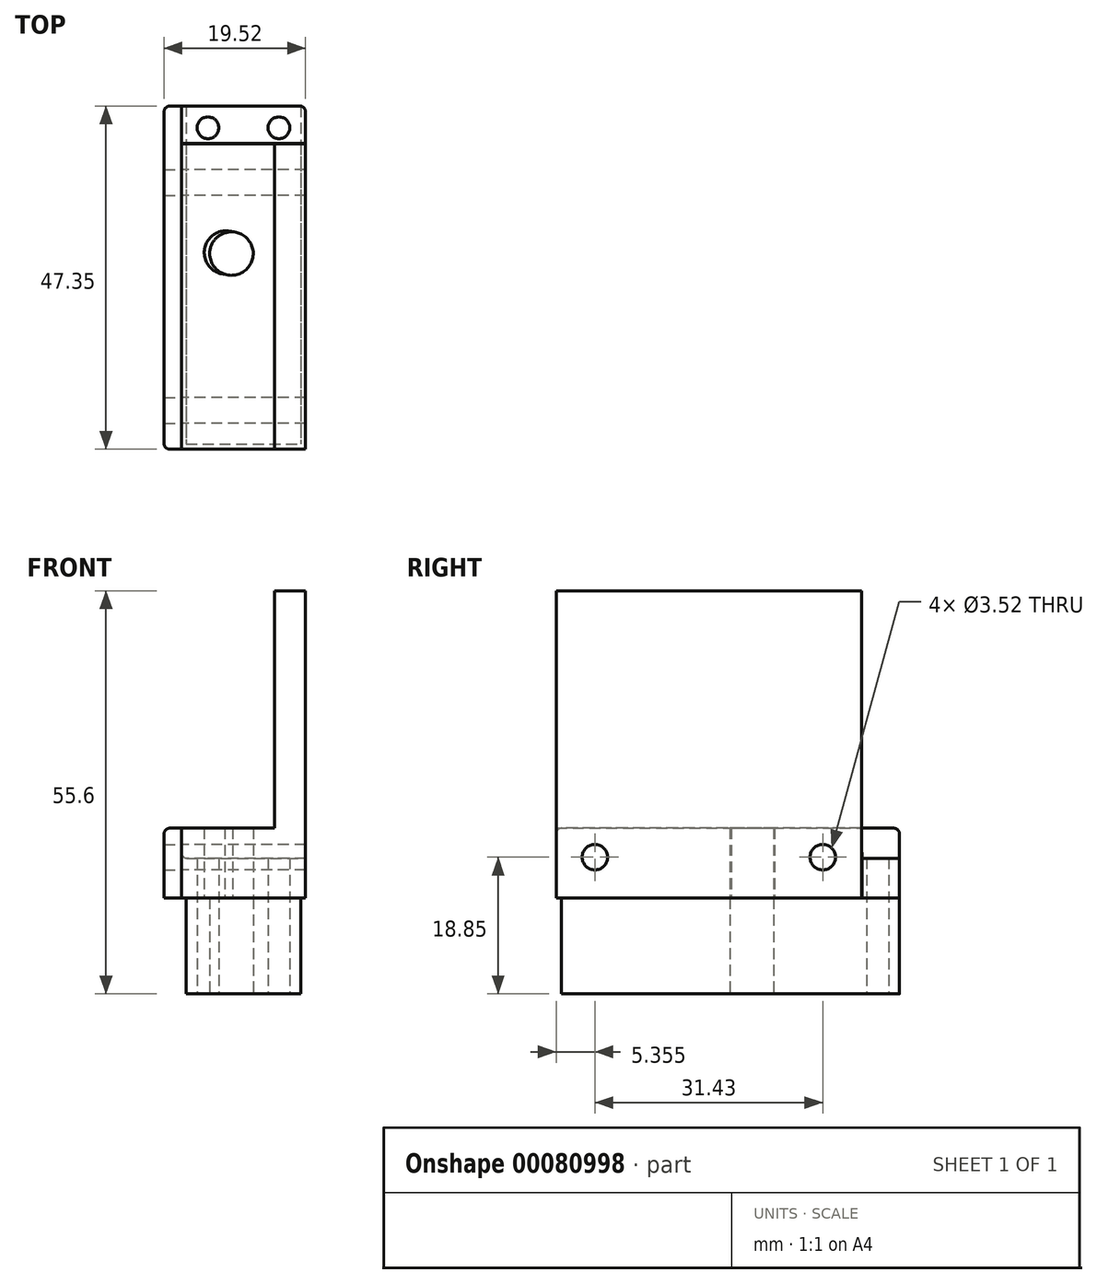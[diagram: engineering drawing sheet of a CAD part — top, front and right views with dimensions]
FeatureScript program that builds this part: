
annotation { "Feature Type Name" : "Feature", "Feature Type Description" : "" }
export const myFeature = defineFeature(function(context is Context, id is Id, definition is map)
    precondition{}
    {
        {
            var Q0;
            Q0=qCreatedBy(makeId("Top.planeOp"),FACE);
            var sketch = newSketch(context, id + "F0", { "sketchPlane" : qUnion([Q0])});
            skLineSegment(sketch, "E0.bottom", {"start": v(-8.56, 21.06) * mm, "end": v(8.56, 21.06) * mm});
            skLineSegment(sketch, "E0.top", {"start": v(-8.56, -21.07) * mm, "end": v(8.55, -21.07) * mm});
            skLineSegment(sketch, "E0.left", {"start": v(-8.56, 21.06) * mm, "end": v(-8.56, -21.07) * mm});
            skLineSegment(sketch, "E0.right", {"start": v(8.56, 21.06) * mm, "end": v(8.55, -21.07) * mm});
            skLineSegment(sketch, "E1", {"start": v(-8.55, 21.06) * mm, "end": v(8.56, -21.07) * mm, "construction": true});
            skSolve(sketch);
        }
        {
            var Q0;
            Q0=makeQuery(id+"F0.imprint","IMPRINT",FACE,{"disambiguationData":[TD([[makeQuery(id+"F0.imprint","IMPRINT",EDGE,{"derivedFrom":sQuery(id+"F0.wireOp",EDGE,"E0.bottom")}),-1.0]])]});
            extrude(context, id + "F1", {"entities" : qUnion([Q0]), "depth" : 9.65 * mm});
        }
        {
            var Q0;
            Q0=makeQuery(id+"F1.opExtrude","SWEPT_FACE",FACE,{"disambiguationData":[OSD([sQuery(id+"F0.wireOp",EDGE,"E0.left")])]});
            var sketch = newSketch(context, id + "F2", { "sketchPlane" : qUnion([Q0])});
            skCircle(sketch, "E2", {"center": v(-15.71, 5.65) * mm, "radius": 1.76 * mm});
            skLineSegment(sketch, "E3", {"start": v(0, 9.65) * mm, "end": v(0, 0) * mm, "construction": true});
            skCircle(sketch, "E4.MirrorC", {"center": v(15.71, 5.65) * mm, "radius": 1.76 * mm});
            skSolve(sketch);
        }
        {
            var Q0;
            Q0=makeQuery(id+"F1.opExtrude","SWEPT_FACE",FACE,{"disambiguationData":[OSD([sQuery(id+"F0.wireOp",EDGE,"E0.right")])]});
            var sketch = newSketch(context, id + "F3", { "sketchPlane" : qUnion([Q0])});
            skPoint(sketch, "E5", {"position": v(-21.07, 0) * mm});
            skPoint(sketch, "E6", {"position": v(21.06, 0) * mm});
            skLineSegment(sketch, "E7.bottom", {"start": v(-21.07, 0) * mm, "end": v(21.07, 0) * mm});
            skLineSegment(sketch, "E7.top", {"start": v(-21.07, 42.4) * mm, "end": v(21.06, 42.4) * mm});
            skLineSegment(sketch, "E7.left", {"start": v(-21.07, 0) * mm, "end": v(-21.07, 42.4) * mm});
            skLineSegment(sketch, "E7.right", {"start": v(21.06, 0) * mm, "end": v(21.06, 42.4) * mm});
            skSolve(sketch);
        }
        {
            var Q0;
            Q0 = qSketchRegion(id + "F3", true);
            extrude(context, id + "F4", {"entities" : qUnion([Q0]), "operationType" : NewBodyOperationType.ADD, "oppositeDirection" : true, "depth" : 4.25 * mm});
        }
        {
            var Q0;
            Q0 = qSketchRegion(id + "F2", true);
            extrude(context, id + "F5", {"entities" : qUnion([Q0]), "operationType" : NewBodyOperationType.REMOVE, "endBound" : BoundingType.THROUGH_ALL, "oppositeDirection" : true, "depth" : 25 * mm});
        }
        {
            var Q0;
            Q0=makeQuery(id+"F1.opExtrude","CAP_FACE",FACE,{"disambiguationData":[OSD([sQuery(id+"F0.wireOp",EDGE,"E0.bottom"),sQuery(id+"F0.wireOp",EDGE,"E0.top"),sQuery(id+"F0.wireOp",EDGE,"E0.left"),sQuery(id+"F0.wireOp",EDGE,"E0.right")])],"isStart":true});
            var sketch = newSketch(context, id + "F6", { "sketchPlane" : qUnion([Q0])});
            skCircle(sketch, "E8", {"center": v(-2.4, -6.06) * mm, "radius": 3 * mm});
            skSolve(sketch);
        }
        {
            var Q0;
            Q0 = qSketchRegion(id + "F6", true);
            extrude(context, id + "F7", {"entities" : qUnion([Q0]), "operationType" : NewBodyOperationType.REMOVE, "oppositeDirection" : true, "depth" : 25 * mm});
        }
        {
            var Q0;
            Q0=qCreatedBy(makeId("Top.planeOp"),FACE);
            var sketch = newSketch(context, id + "F8", { "sketchPlane" : qUnion([Q0])});
            skLineSegment(sketch, "E9.bottom", {"start": v(-7.9, 26.28) * mm, "end": v(7.9, 26.28) * mm});
            skLineSegment(sketch, "E9.top", {"start": v(-7.9, -20.32) * mm, "end": v(7.9, -20.32) * mm});
            skLineSegment(sketch, "E9.left", {"start": v(-7.9, 26.28) * mm, "end": v(-7.9, -20.32) * mm});
            skLineSegment(sketch, "E9.right", {"start": v(7.9, 26.28) * mm, "end": v(7.9, -20.32) * mm});
            skSolve(sketch);
        }
        {
            var Q0;
            Q0 = qSketchRegion(id + "F8", true);
            extrude(context, id + "F9", {"entities" : qUnion([Q0]), "oppositeDirection" : true, "depth" : 13.2 * mm});
        }
        {
            var Q0;
            Q0=makeQuery(id+"F9.opExtrude","CAP_FACE",FACE,{"disambiguationData":[OSD([sQuery(id+"F8.wireOp",EDGE,"E9.bottom"),sQuery(id+"F8.wireOp",EDGE,"E9.top"),sQuery(id+"F8.wireOp",EDGE,"E9.left"),sQuery(id+"F8.wireOp",EDGE,"E9.right")])],"isStart":false});
            var sketch = newSketch(context, id + "F10", { "sketchPlane" : qUnion([Q0])});
            skCircle(sketch, "E10", {"center": v(-1.65, -5.93) * mm, "radius": 3 * mm});
            skCircle(sketch, "E11", {"center": v(-4.9, -23.28) * mm, "radius": 1.5 * mm});
            skLineSegment(sketch, "E12", {"start": v(0, 20.32) * mm, "end": v(0, -26.28) * mm, "construction": true});
            skCircle(sketch, "E13.MirrorC", {"center": v(4.9, -23.28) * mm, "radius": 1.5 * mm});
            skSolve(sketch);
        }
        {
            var Q0;
            Q0 = qSketchRegion(id + "F10", true);
            extrude(context, id + "F11", {"entities" : qUnion([Q0]), "operationType" : NewBodyOperationType.REMOVE, "oppositeDirection" : true, "depth" : 25 * mm});
        }
        {
            var Q0;
            Q0=makeQuery(id+"F1.opExtrude","SWEPT_FACE",FACE,{"disambiguationData":[OSD([sQuery(id+"F0.wireOp",EDGE,"E0.left")])]});
            var sketch = newSketch(context, id + "F12", { "sketchPlane" : qUnion([Q0])});
            skPoint(sketch, "E14.0", {"position": v(-26.28, 0) * mm});
            skLineSegment(sketch, "E15.bottom", {"start": v(21.07, 0) * mm, "end": v(-26.28, 0) * mm});
            skLineSegment(sketch, "E15.top", {"start": v(21.07, 9.65) * mm, "end": v(-26.28, 9.65) * mm});
            skLineSegment(sketch, "E15.left", {"start": v(21.07, 0) * mm, "end": v(21.07, 9.65) * mm});
            skLineSegment(sketch, "E15.right", {"start": v(-26.28, 0) * mm, "end": v(-26.28, 9.65) * mm});
            skCircle(sketch, "E16.0", {"center": v(-15.71, 5.65) * mm, "radius": 1.76 * mm});
            skCircle(sketch, "E16.1", {"center": v(15.71, 5.65) * mm, "radius": 1.76 * mm});
            skSolve(sketch);
        }
        {
            var Q0;
            {var subQ0=sQuery(id+"F12.wireOp",EDGE,"E15.left");Q0=makeQuery(id+"F12.imprint","IMPRINT",FACE,{"disambiguationData":[TD([[makeQuery(id+"F12.imprint","IMPRINT",EDGE,{"derivedFrom":subQ0}),-1.0]])]});}
            var Q1;
            {var subQ2=sQuery(id+"F12.wireOp",EDGE,"E15.right");Q1=makeQuery(id+"F12.imprint","IMPRINT",FACE,{"disambiguationData":[TD([[makeQuery(id+"F12.imprint","IMPRINT",EDGE,{"derivedFrom":subQ2}),-1.0]])]});}
            var Q2;
            Q2 = qSketchRegion(id + "F12", true);
            extrude(context, id + "F13", {"entities" : qUnion([Q0, Q1, Q2]), "depth" : (0.4 * 6) * mm});
        }
        {
            var Q0;
            Q0=makeQuery(id+"F13.opExtrude","CAP_FACE",FACE,{"disambiguationData":[OSD([sQuery(id+"F12.wireOp",EDGE,"E15.bottom"),sQuery(id+"F12.wireOp",EDGE,"E15.top"),sQuery(id+"F12.wireOp",EDGE,"E15.left"),sQuery(id+"F12.wireOp",EDGE,"E15.right"),sQuery(id+"F12.wireOp",EDGE,"E16.0"),sQuery(id+"F12.wireOp",EDGE,"E16.1")])],"isStart":true});
            var sketch = newSketch(context, id + "F14", { "sketchPlane" : qUnion([Q0])});
            skLineSegment(sketch, "E17.bottom", {"start": v(26.28, 9.65) * mm, "end": v(21.14, 9.65) * mm});
            skLineSegment(sketch, "E17.top", {"start": v(26.28, 0) * mm, "end": v(21.14, 0) * mm});
            skLineSegment(sketch, "E17.left", {"start": v(26.28, 9.65) * mm, "end": v(26.28, 0) * mm});
            skLineSegment(sketch, "E17.right", {"start": v(21.14, 9.65) * mm, "end": v(21.14, 0) * mm});
            skSolve(sketch);
        }
        {
            var Q0;
            Q0 = qSketchRegion(id + "F14", true);
            var Q1;
            Q1=makeQuery(id+"F4.boolean.opBoolean","MERGE",FACE,{"derivedFrom":[makeQuery(id+"F1.opExtrude","SWEPT_FACE",FACE,{"disambiguationData":[OSD([sQuery(id+"F0.wireOp",EDGE,"E0.right")])]}),makeQuery(id+"F4.opExtrude","CAP_FACE",FACE,{"disambiguationData":[OSD([sQuery(id+"F3.wireOp",EDGE,"E7.bottom"),sQuery(id+"F3.wireOp",EDGE,"E7.top"),sQuery(id+"F3.wireOp",EDGE,"E7.left"),sQuery(id+"F3.wireOp",EDGE,"E7.right")])],"isStart":true})]});
            extrude(context, id + "F15", {"entities" : qUnion([Q0]), "operationType" : NewBodyOperationType.ADD, "endBound" : BoundingType.UP_TO_SURFACE, "endBoundEntityFace" : qUnion([Q1]), "depth" : 25 * mm});
        }
        {
            var Q0;
            Q0=makeQuery(id+"F15.boolean.opBoolean","MERGE",FACE,{"derivedFrom":[makeQuery(id+"F13.opExtrude","SWEPT_FACE",FACE,{"disambiguationData":[OSD([sQuery(id+"F12.wireOp",EDGE,"E15.top")])]}),makeQuery(id+"F15.opExtrude","SWEPT_FACE",FACE,{"disambiguationData":[OSD([sQuery(id+"F14.wireOp",EDGE,"E17.bottom")])]})]});
            var sketch = newSketch(context, id + "F16", { "sketchPlane" : qUnion([Q0])});
            skCircle(sketch, "E18.0", {"center": v(-4.9, 23.28) * mm, "radius": 1.5 * mm});
            skCircle(sketch, "E18.1", {"center": v(4.9, 23.28) * mm, "radius": 1.5 * mm});
            skSolve(sketch);
        }
        {
            var Q0;
            Q0 = qSketchRegion(id + "F16", true);
            extrude(context, id + "F17", {"entities" : qUnion([Q0]), "operationType" : NewBodyOperationType.REMOVE, "oppositeDirection" : true, "depth" : 25 * mm});
        }
        {
            var Q0;
            Q0=makeQuery(id+"F15.boolean.opBoolean","MERGE",FACE,{"derivedFrom":[makeQuery(id+"F13.opExtrude","SWEPT_FACE",FACE,{"disambiguationData":[OSD([sQuery(id+"F12.wireOp",EDGE,"E15.top")])]}),makeQuery(id+"F15.opExtrude","SWEPT_FACE",FACE,{"disambiguationData":[OSD([sQuery(id+"F14.wireOp",EDGE,"E17.bottom")])]})]});
            var sketch = newSketch(context, id + "F18", { "sketchPlane" : qUnion([Q0])});
            skLineSegment(sketch, "E19.bottom", {"start": v(-8.55, 21.14) * mm, "end": v(8.56, 21.14) * mm});
            skLineSegment(sketch, "E19.top", {"start": v(-8.55, 26.28) * mm, "end": v(8.56, 26.28) * mm});
            skLineSegment(sketch, "E19.left", {"start": v(-8.56, 21.14) * mm, "end": v(-8.56, 26.28) * mm});
            skLineSegment(sketch, "E19.right", {"start": v(8.56, 21.14) * mm, "end": v(8.56, 26.28) * mm});
            skSolve(sketch);
        }
        {
            var Q0;
            Q0 = qSketchRegion(id + "F18", true);
            extrude(context, id + "F19", {"entities" : qUnion([Q0]), "operationType" : NewBodyOperationType.REMOVE, "oppositeDirection" : true, "depth" : (9.65 - 5.5) * mm});
        }
        {
            var Q0;
            Q0=makeQuery(id+"F19.boolean.opBoolean","COPY",EDGE,{"derivedFrom":makeQuery(id+"F19.opExtrude","CAP_EDGE",EDGE,{"disambiguationData":[OSD([sQuery(id+"F18.wireOp",EDGE,"E19.right")])],"isStart":false})});
            var Q1;
            Q1=makeQuery(id+"F19.boolean.opBoolean","COPY",EDGE,{"derivedFrom":makeQuery(id+"F19.opExtrude","CAP_EDGE",EDGE,{"disambiguationData":[OSD([sQuery(id+"F18.wireOp",EDGE,"E19.top")])],"isStart":false})});
            var Q2;
            Q2=makeQuery(id+"F19.boolean.opBoolean","COPY",EDGE,{"derivedFrom":makeQuery(id+"F19.opExtrude","CAP_EDGE",EDGE,{"disambiguationData":[OSD([sQuery(id+"F18.wireOp",EDGE,"E19.left")])],"isStart":false})});
            var Q3;
            Q3=makeQuery(id+"F19.boolean.opBoolean","COPY",EDGE,{"derivedFrom":makeQuery(id+"F19.opExtrude","SWEPT_EDGE",EDGE,{"disambiguationData":[OSD([sQuery(id+"F12.wireOp",EDGE,"E15.top"),sQuery(id+"F12.wireOp",EDGE,"E15.right"),sQuery(id+"F14.wireOp",EDGE,"E17.bottom"),sQuery(id+"F14.wireOp",EDGE,"E17.left"),sQuery(id+"F18.wireOp",EDGE,"E19.top"),sQuery(id+"F18.wireOp",EDGE,"E19.left")])]})});
            var Q4;
            Q4=makeQuery(id+"F15.boolean.opBoolean","MERGE",EDGE,{"derivedFrom":[makeQuery(id+"F13.opExtrude","SWEPT_EDGE",EDGE,{"disambiguationData":[OSD([sQuery(id+"F12.wireOp",EDGE,"E15.top"),sQuery(id+"F12.wireOp",EDGE,"E15.right")])]}),makeQuery(id+"F15.opExtrude","SWEPT_EDGE",EDGE,{"disambiguationData":[OSD([sQuery(id+"F14.wireOp",EDGE,"E17.bottom"),sQuery(id+"F14.wireOp",EDGE,"E17.left")])]})]});
            var Q5;
            Q5=makeQuery(id+"F13.opExtrude","CAP_EDGE",EDGE,{"disambiguationData":[OSD([sQuery(id+"F12.wireOp",EDGE,"E15.top")])],"isStart":false});
            var Q6;
            Q6=makeQuery(id+"F13.opExtrude","CAP_EDGE",EDGE,{"disambiguationData":[OSD([sQuery(id+"F12.wireOp",EDGE,"E15.left")])],"isStart":false});
            var Q7;
            Q7=makeQuery(id+"F13.opExtrude","SWEPT_EDGE",EDGE,{"disambiguationData":[OSD([sQuery(id+"F12.wireOp",EDGE,"E15.top"),sQuery(id+"F12.wireOp",EDGE,"E15.left")])]});
            var Q8;
            Q8=makeQuery(id+"F15.opExtrude","CAP_EDGE",EDGE,{"disambiguationData":[OSD([sQuery(id+"F14.wireOp",EDGE,"E17.left")])],"isStart":false});
            var Q9;
            Q9=makeQuery(id+"F13.opExtrude","CAP_EDGE",EDGE,{"disambiguationData":[OSD([sQuery(id+"F12.wireOp",EDGE,"E15.right")])],"isStart":false});
            fillet(context, id + "F20", {"entities" : qUnion([Q0, Q1, Q2, Q3, Q4, Q5, Q6, Q7, Q8, Q9]), "radius" : 0.8 * mm, "tangentPropagation" : true, "allowEdgeOverflow" : false});
        }
    });
